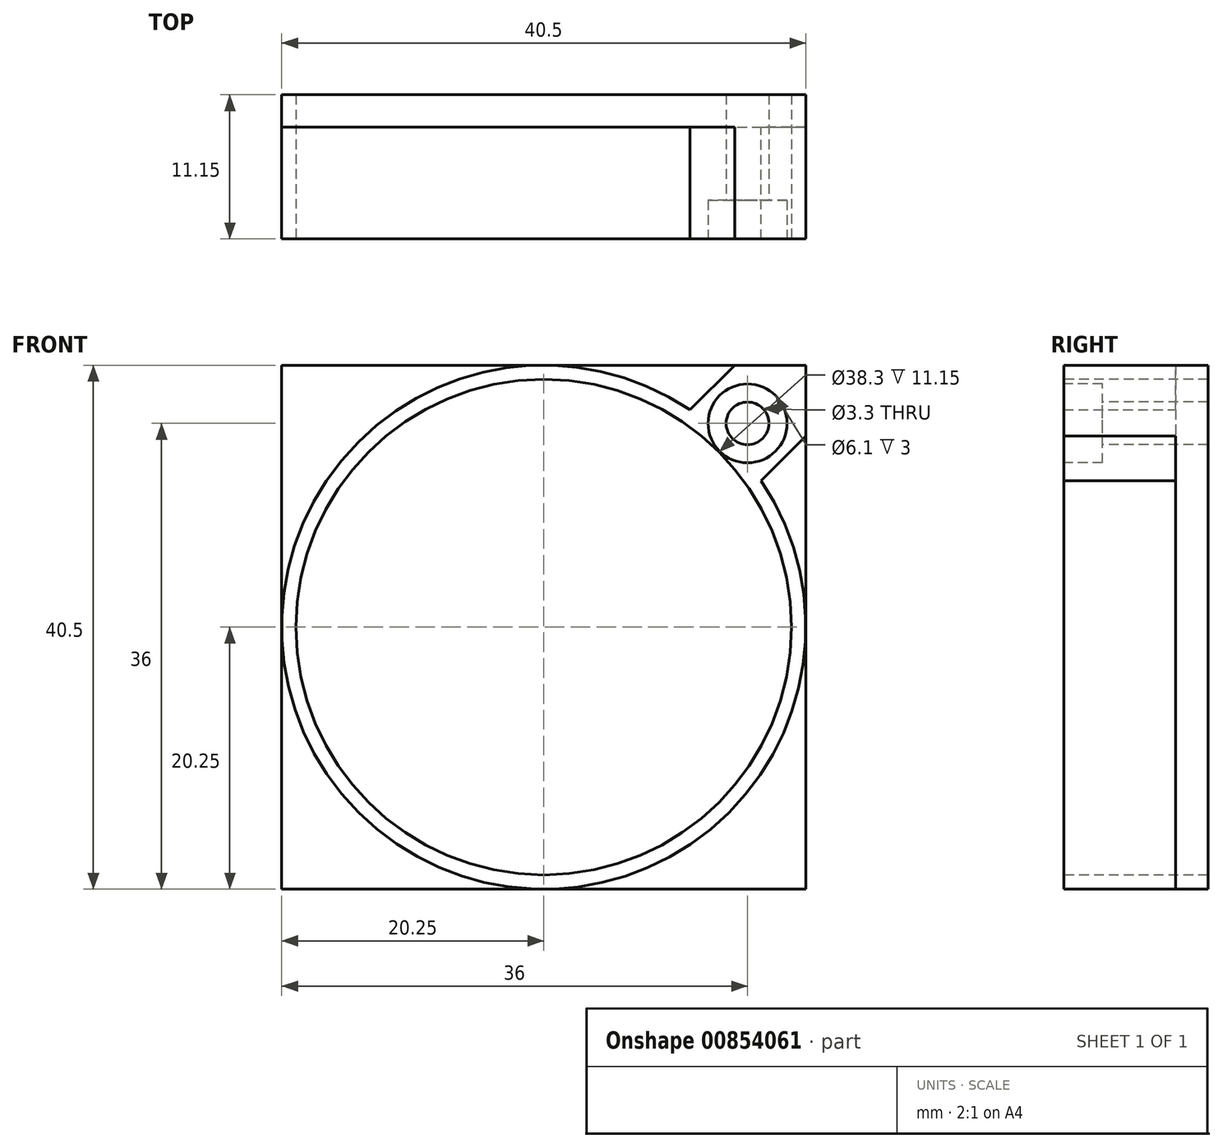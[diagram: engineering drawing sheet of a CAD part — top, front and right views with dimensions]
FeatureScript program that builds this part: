
annotation { "Feature Type Name" : "Feature", "Feature Type Description" : "" }
export const myFeature = defineFeature(function(context is Context, id is Id, definition is map)
    precondition{}
    {
        {
            var Q0;
            Q0=qCreatedBy(makeId("Front.planeOp"),FACE);
            var sketch = newSketch(context, id + "F0", { "sketchPlane" : qUnion([Q0])});
            skLineSegment(sketch, "E0.bottom", {"start": v(0, 0) * mm, "end": v(40.5, 0) * mm});
            skLineSegment(sketch, "E0.top", {"start": v(0, 40.5) * mm, "end": v(40.5, 40.5) * mm});
            skLineSegment(sketch, "E0.left", {"start": v(0, 0) * mm, "end": v(0, 40.5) * mm});
            skLineSegment(sketch, "E0.right", {"start": v(40.5, 0) * mm, "end": v(40.5, 40.5) * mm});
            skSolve(sketch);
        }
        {
            var Q0;
            Q0=makeQuery(id+"F0.imprint","IMPRINT",FACE,{"disambiguationData":[TD([[makeQuery(id+"F0.imprint","IMPRINT",EDGE,{"derivedFrom":sQuery(id+"F0.wireOp",EDGE,"E0.bottom")}),1.0]])]});
            extrude(context, id + "F1", {"entities" : qUnion([Q0]), "depth" : 2.5 * mm, "offsetDistance" : 25 * mm});
        }
        {
            var Q0;
            Q0=makeQuery(id+"F1.opExtrude","CAP_FACE",FACE,{"disambiguationData":[OSD([sQuery(id+"F0.wireOp",EDGE,"E0.bottom"),sQuery(id+"F0.wireOp",EDGE,"E0.top"),sQuery(id+"F0.wireOp",EDGE,"E0.left"),sQuery(id+"F0.wireOp",EDGE,"E0.right")])],"isStart":false});
            var sketch = newSketch(context, id + "F2", { "sketchPlane" : qUnion([Q0])});
            skCircle(sketch, "E1", {"center": v(20.25, 20.25) * mm, "radius": 20.25 * mm});
            skPoint(sketch, "E1.centerSnap0", {"position": v(40.5, 20.25) * mm});
            skPoint(sketch, "E1.centerSnap1", {"position": v(20.25, 40.5) * mm});
            skLineSegment(sketch, "E2", {"start": v(20.25, 20.25) * mm, "end": v(40.5, 40.5) * mm, "construction": true});
            skLineSegment(sketch, "E3", {"start": v(31.56, 37.04) * mm, "end": v(35.02, 40.5) * mm});
            skLineSegment(sketch, "E4", {"start": v(37.04, 31.56) * mm, "end": v(40.5, 35.02) * mm});
            skSolve(sketch);
        }
        {
            var Q0;
            {var subQ0=sQuery(id+"F2.wireOp",EDGE,"E1");var subQ4=makeQuery(id+"F2.imprint","INTERSECT",VERTEX,{"derivedFrom":[subQ0,sQuery(id+"F2.wireOp",EDGE,"E4")]});Q0=makeQuery(id+"F2.imprint","IMPRINT",FACE,{"disambiguationData":[TD([[makeQuery(id+"F2.imprint","IMPRINT",EDGE,{"disambiguationData":[TD([[subQ4,1.0]])],"derivedFrom":subQ0}),1.0]])]});}
            extrude(context, id + "F3", {"entities" : qUnion([Q0]), "operationType" : NewBodyOperationType.ADD, "depth" : 8.65 * mm, "offsetDistance" : 25 * mm});
        }
        {
            var Q0;
            {var subQ3=sQuery(id+"F2.wireOp",EDGE,"E3");Q0=makeQuery(id+"F2.imprint","IMPRINT",FACE,{"disambiguationData":[TD([[makeQuery(id+"F2.imprint","IMPRINT",EDGE,{"derivedFrom":subQ3}),-1.0]])]});}
            var Q1;
            Q1=makeQuery(id+"F3.opExtrude","CAP_FACE",FACE,{"disambiguationData":[OSD([sQuery(id+"F2.wireOp",EDGE,"E1")])],"isStart":false});
            extrude(context, id + "F4", {"entities" : qUnion([Q0]), "operationType" : NewBodyOperationType.ADD, "endBound" : BoundingType.UP_TO_SURFACE, "depth" : 25 * mm, "endBoundEntityFace" : qUnion([Q1]), "offsetDistance" : 25 * mm});
        }
        {
            var Q0;
            {var subQ0=sQuery(id+"F2.wireOp",EDGE,"E1");Q0=makeQuery(id+"FD1Ip4M6UQZEetG_1.3.F4.boolean.opBoolean","MERGE",FACE,{"derivedFrom":[makeQuery(id+"FD1Ip4M6UQZEetG_1.2.F4.boolean.opBoolean","MERGE",FACE,{"derivedFrom":[makeQuery(id+"FD1Ip4M6UQZEetG_1.1.F4.boolean.opBoolean","MERGE",FACE,{"derivedFrom":[makeQuery(id+"F4.boolean.opBoolean","MERGE",FACE,{"derivedFrom":[makeQuery(id+"F3.opExtrude","CAP_FACE",FACE,{"disambiguationData":[OSD([subQ0])],"isStart":false}),makeQuery(id+"F4.opExtrude","CAP_FACE",FACE,{"disambiguationData":[OSD([subQ0])],"isStart":false})]}),makeQuery(id+"FD1Ip4M6UQZEetG_1.1.F4.opExtrude","CAP_FACE",FACE,{"disambiguationData":[OSD([subQ0])],"isStart":false})]}),makeQuery(id+"FD1Ip4M6UQZEetG_1.2.F4.opExtrude","CAP_FACE",FACE,{"disambiguationData":[OSD([subQ0])],"isStart":false})]}),makeQuery(id+"FD1Ip4M6UQZEetG_1.3.F4.opExtrude","CAP_FACE",FACE,{"disambiguationData":[OSD([subQ0])],"isStart":false})]});}
            var sketch = newSketch(context, id + "F5", { "sketchPlane" : qUnion([Q0])});
            skCircle(sketch, "E5.0", {"center": v(20.25, 20.25) * mm, "radius": 19.15 * mm});
            skSolve(sketch);
        }
        {
            var Q0;
            Q0=makeQuery(id+"F5.imprint","IMPRINT",FACE,{"disambiguationData":[TD([[makeQuery(id+"F5.imprint","IMPRINT",EDGE,{"derivedFrom":sQuery(id+"F5.wireOp",EDGE,"E5.0")}),1.0]])]});
            extrude(context, id + "F6", {"entities" : qUnion([Q0]), "operationType" : NewBodyOperationType.REMOVE, "endBound" : BoundingType.THROUGH_ALL, "oppositeDirection" : true, "depth" : 25 * mm, "offsetDistance" : 25 * mm});
        }
        {
            var Q0;
            {var subQ0=sQuery(id+"F2.wireOp",EDGE,"E1");Q0=makeQuery(id+"FD1Ip4M6UQZEetG_1.3.F4.boolean.opBoolean","MERGE",FACE,{"derivedFrom":[makeQuery(id+"FD1Ip4M6UQZEetG_1.2.F4.boolean.opBoolean","MERGE",FACE,{"derivedFrom":[makeQuery(id+"FD1Ip4M6UQZEetG_1.1.F4.boolean.opBoolean","MERGE",FACE,{"derivedFrom":[makeQuery(id+"F4.boolean.opBoolean","MERGE",FACE,{"derivedFrom":[makeQuery(id+"F3.opExtrude","CAP_FACE",FACE,{"disambiguationData":[OSD([subQ0])],"isStart":false}),makeQuery(id+"F4.opExtrude","CAP_FACE",FACE,{"disambiguationData":[OSD([subQ0])],"isStart":false})]}),makeQuery(id+"FD1Ip4M6UQZEetG_1.1.F4.opExtrude","CAP_FACE",FACE,{"disambiguationData":[OSD([subQ0])],"isStart":false})]}),makeQuery(id+"FD1Ip4M6UQZEetG_1.2.F4.opExtrude","CAP_FACE",FACE,{"disambiguationData":[OSD([subQ0])],"isStart":false})]}),makeQuery(id+"FD1Ip4M6UQZEetG_1.3.F4.opExtrude","CAP_FACE",FACE,{"disambiguationData":[OSD([subQ0])],"isStart":false})]});}
            var sketch = newSketch(context, id + "F7", { "sketchPlane" : qUnion([Q0])});
            skPoint(sketch, "E6", {"position": v(36, 36) * mm});
            skSolve(sketch);
        }
        {
            var Q0;
            Q0=sQuery(id+"F7.wireOp",VERTEX,"E6");
            var Q1;
            Q1=makeQuery(id+"F1.opExtrude","SWEPT_BODY",BODY,{"disambiguationData":[OSD([sQuery(id+"F0.wireOp",EDGE,"E0.bottom"),sQuery(id+"F0.wireOp",EDGE,"E0.top"),sQuery(id+"F0.wireOp",EDGE,"E0.left"),sQuery(id+"F0.wireOp",EDGE,"E0.right")])]});
            hole(context, id + "F8", {"style" : HoleStyle.C_BORE, "endStyle" : HoleEndStyle.THROUGH, "holeDiameter" : 3.3 * mm, "cBoreDiameter" : 6.1 * mm, "cBoreDepth" : 3 * mm, "majorDiameter" : 5 * mm, "isTappedThrough" : true, "tappedDepth" : 12 * mm, "tapClearance" : 3, "locations" : qUnion([Q0]), "scope" : qUnion([Q1])});
        }
    });
